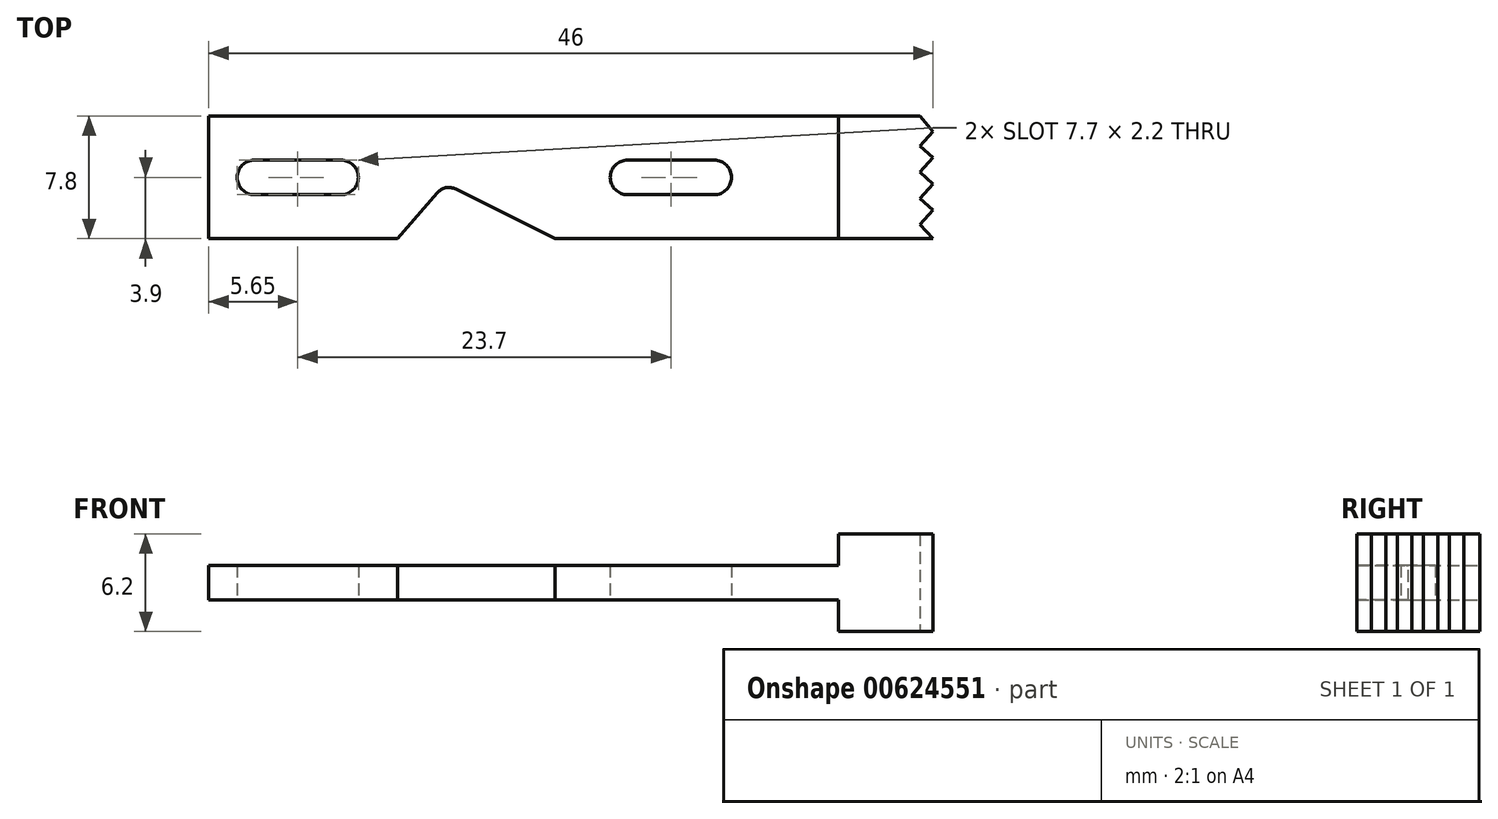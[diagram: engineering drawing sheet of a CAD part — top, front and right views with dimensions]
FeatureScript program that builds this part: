
annotation { "Feature Type Name" : "Feature", "Feature Type Description" : "" }
export const myFeature = defineFeature(function(context is Context, id is Id, definition is map)
    precondition{}
    {
        {
            var Q0;
            Q0=qCreatedBy(makeId("Top.planeOp"),FACE);
            var sketch = newSketch(context, id + "F0", { "sketchPlane" : qUnion([Q0])});
            skLineSegment(sketch, "E0.bottom", {"start": v(0, 0) * mm, "end": v(40, 0) * mm});
            skLineSegment(sketch, "E0.top", {"start": v(0, 7.8) * mm, "end": v(40, 7.8) * mm});
            skLineSegment(sketch, "E0.left", {"start": v(0, 0) * mm, "end": v(0, 7.8) * mm});
            skLineSegment(sketch, "E0.right", {"start": v(40, 0) * mm, "end": v(40, 7.8) * mm});
            skSolve(sketch);
        }
        {
            var Q0;
            Q0 = qSketchRegion(id + "F0", true);
            extrude(context, id + "F1", {"entities" : qUnion([Q0]), "depth" : 2.2 * mm, "offsetDistance" : 25 * mm});
        }
        {
            var Q0;
            Q0=makeQuery(id+"F1.opExtrude","SWEPT_FACE",FACE,{"disambiguationData":[OSD([sQuery(id+"F0.wireOp",EDGE,"E0.right")])]});
            var sketch = newSketch(context, id + "F2", { "sketchPlane" : qUnion([Q0])});
            skLineSegment(sketch, "E1.bottom", {"start": v(0, 4.2) * mm, "end": v(7.8, 4.2) * mm});
            skLineSegment(sketch, "E1.top", {"start": v(0, -2) * mm, "end": v(7.8, -2) * mm});
            skLineSegment(sketch, "E1.left", {"start": v(0, 4.2) * mm, "end": v(0, -2) * mm});
            skLineSegment(sketch, "E1.right", {"start": v(7.8, 4.2) * mm, "end": v(7.8, -2) * mm});
            skSolve(sketch);
        }
        {
            var Q0;
            Q0 = qSketchRegion(id + "F2", true);
            extrude(context, id + "F3", {"entities" : qUnion([Q0]), "operationType" : NewBodyOperationType.ADD, "depth" : 6 * mm, "offsetDistance" : 25 * mm});
        }
        {
            var Q0;
            Q0=makeQuery(id+"F3.opExtrude","SWEPT_FACE",FACE,{"disambiguationData":[OSD([sQuery(id+"F2.wireOp",EDGE,"E1.top")])]});
            var sketch = newSketch(context, id + "F4", { "sketchPlane" : qUnion([Q0])});
            skLineSegment(sketch, "E2", {"start": v(46, 0) * mm, "end": v(45.18, -0.9) * mm});
            skLineSegment(sketch, "E3", {"start": v(45.18, -0.9) * mm, "end": v(46, -1.83) * mm});
            skLineSegment(sketch, "E4", {"start": v(46, -1.83) * mm, "end": v(45.18, -2.57) * mm});
            skLineSegment(sketch, "E5", {"start": v(45.18, -2.57) * mm, "end": v(46, -3.49) * mm});
            skLineSegment(sketch, "E6", {"start": v(46, -3.49) * mm, "end": v(45.18, -4.22) * mm});
            skLineSegment(sketch, "E7", {"start": v(45.18, -4.22) * mm, "end": v(46, -5.14) * mm});
            skLineSegment(sketch, "E8", {"start": v(46, -5.14) * mm, "end": v(45.18, -5.88) * mm});
            skLineSegment(sketch, "E9", {"start": v(45.18, -5.88) * mm, "end": v(46, -6.8) * mm});
            skLineSegment(sketch, "E10", {"start": v(46, -6.8) * mm, "end": v(45.18, -7.8) * mm});
            skLineSegment(sketch, "E11", {"start": v(45.18, -7.8) * mm, "end": v(46, -7.8) * mm});
            skLineSegment(sketch, "E12", {"start": v(46, -7.8) * mm, "end": v(46, 0) * mm});
            skSolve(sketch);
        }
        {
            var Q0;
            Q0 = qSketchRegion(id + "F4", true);
            extrude(context, id + "F5", {"entities" : qUnion([Q0]), "operationType" : NewBodyOperationType.REMOVE, "oppositeDirection" : true, "depth" : 25 * mm, "offsetDistance" : 25 * mm});
        }
        {
            var Q0;
            Q0=makeQuery(id+"F1.opExtrude","CAP_FACE",FACE,{"disambiguationData":[OSD([sQuery(id+"F0.wireOp",EDGE,"E0.bottom"),sQuery(id+"F0.wireOp",EDGE,"E0.top"),sQuery(id+"F0.wireOp",EDGE,"E0.left"),sQuery(id+"F0.wireOp",EDGE,"E0.right")])],"isStart":true});
            var sketch = newSketch(context, id + "F6", { "sketchPlane" : qUnion([Q0])});
            skLineSegment(sketch, "E13", {"start": v(15, -3.5) * mm, "end": v(12, 0) * mm});
            skLineSegment(sketch, "E14", {"start": v(12, 0) * mm, "end": v(22, 0) * mm});
            skLineSegment(sketch, "E15", {"start": v(22, 0) * mm, "end": v(15, -3.5) * mm});
            skSolve(sketch);
        }
        {
            var Q0;
            Q0 = qSketchRegion(id + "F6", true);
            extrude(context, id + "F7", {"entities" : qUnion([Q0]), "operationType" : NewBodyOperationType.REMOVE, "oppositeDirection" : true, "depth" : 25 * mm, "offsetDistance" : 25 * mm});
        }
        {
            var Q0;
            Q0=makeQuery(id+"F7.boolean.opBoolean","COPY",EDGE,{"derivedFrom":makeQuery(id+"F7.opExtrude","SWEPT_EDGE",EDGE,{"disambiguationData":[OSD([sQuery(id+"F6.wireOp",EDGE,"E13"),sQuery(id+"F6.wireOp",EDGE,"E15")])]})});
            fillet(context, id + "F8", {"entities" : qUnion([Q0]), "radius" : 1 * mm, "tangentPropagation" : true, "allowEdgeOverflow" : false});
        }
        {
            var Q0;
            Q0=makeQuery(id+"F1.opExtrude","CAP_FACE",FACE,{"disambiguationData":[OSD([sQuery(id+"F0.wireOp",EDGE,"E0.bottom"),sQuery(id+"F0.wireOp",EDGE,"E0.top"),sQuery(id+"F0.wireOp",EDGE,"E0.left"),sQuery(id+"F0.wireOp",EDGE,"E0.right")])],"isStart":true});
            var sketch = newSketch(context, id + "F9", { "sketchPlane" : qUnion([Q0])});
            skArc(sketch, "E16", {"start": v(2.9, -2.8) * mm, "mid": v(1.8, -3.9) * mm, "end": v(2.9, -5) * mm});
            skArc(sketch, "E17", {"start": v(8.4, -5) * mm, "mid": v(9.5, -3.9) * mm, "end": v(8.4, -2.8) * mm});
            skLineSegment(sketch, "E18", {"start": v(2.9, -5) * mm, "end": v(8.4, -5) * mm});
            skLineSegment(sketch, "E19", {"start": v(2.9, -2.8) * mm, "end": v(8.4, -2.8) * mm});
            skSolve(sketch);
        }
        {
            var Q0;
            Q0 = qSketchRegion(id + "F9", true);
            extrude(context, id + "F10", {"entities" : qUnion([Q0]), "operationType" : NewBodyOperationType.REMOVE, "oppositeDirection" : true, "depth" : 25 * mm, "offsetDistance" : 25 * mm});
        }
        {
            var Q0;
            Q0=makeQuery(id+"F1.opExtrude","CAP_FACE",FACE,{"disambiguationData":[OSD([sQuery(id+"F0.wireOp",EDGE,"E0.bottom"),sQuery(id+"F0.wireOp",EDGE,"E0.top"),sQuery(id+"F0.wireOp",EDGE,"E0.left"),sQuery(id+"F0.wireOp",EDGE,"E0.right")])],"isStart":true});
            var sketch = newSketch(context, id + "F11", { "sketchPlane" : qUnion([Q0])});
            skArc(sketch, "E20", {"start": v(26.6, -2.8) * mm, "mid": v(25.5, -3.9) * mm, "end": v(26.6, -5) * mm});
            skPoint(sketch, "E20.centerSnap0", {"position": v(9.5, -3.9) * mm});
            skArc(sketch, "E21", {"start": v(32.1, -5) * mm, "mid": v(33.2, -3.9) * mm, "end": v(32.1, -2.8) * mm});
            skLineSegment(sketch, "E22", {"start": v(26.6, -2.8) * mm, "end": v(32.1, -2.8) * mm});
            skLineSegment(sketch, "E23", {"start": v(26.6, -5) * mm, "end": v(32.1, -5) * mm});
            skSolve(sketch);
        }
        {
            var Q0;
            Q0 = qSketchRegion(id + "F11", true);
            extrude(context, id + "F12", {"entities" : qUnion([Q0]), "operationType" : NewBodyOperationType.REMOVE, "oppositeDirection" : true, "depth" : 25 * mm, "offsetDistance" : 25 * mm});
        }
    });
